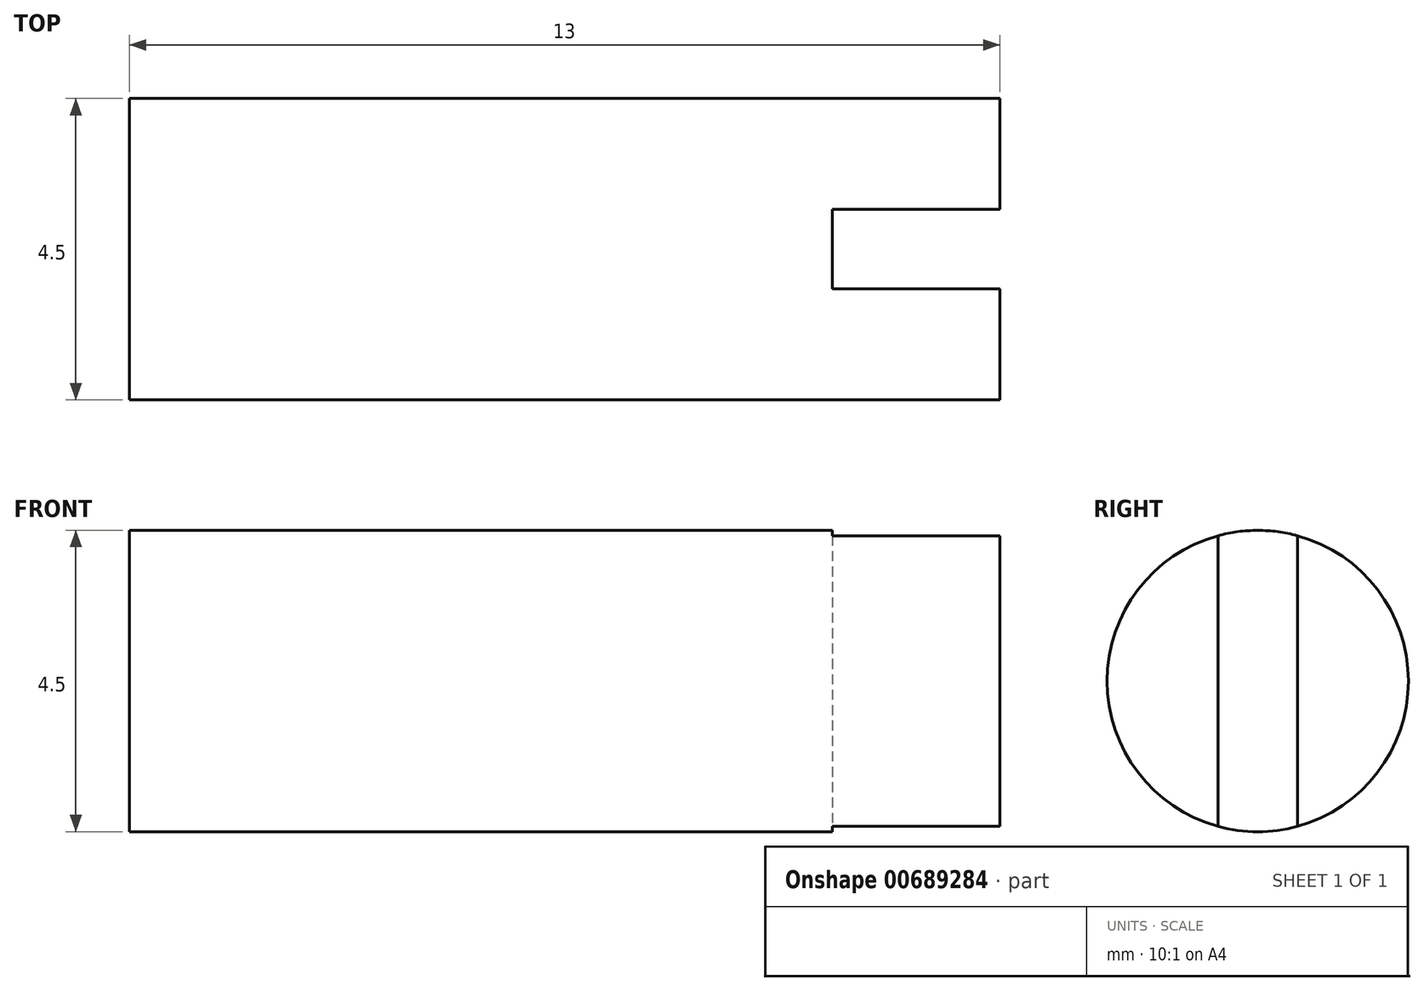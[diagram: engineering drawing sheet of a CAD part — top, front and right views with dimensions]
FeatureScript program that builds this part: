
annotation { "Feature Type Name" : "Feature", "Feature Type Description" : "" }
export const myFeature = defineFeature(function(context is Context, id is Id, definition is map)
    precondition{}
    {
        {
            var Q0;
            Q0=qCreatedBy(makeId("Front.planeOp"),FACE);
            var sketch = newSketch(context, id + "F0", { "sketchPlane" : qUnion([Q0])});
            skLineSegment(sketch, "E0", {"start": v(0, 0) * mm, "end": v(13, 0) * mm});
            skLineSegment(sketch, "E1", {"start": v(13, 0) * mm, "end": v(13, 2.25) * mm});
            skLineSegment(sketch, "E2", {"start": v(13, 2.25) * mm, "end": v(0, 2.25) * mm});
            skLineSegment(sketch, "E3", {"start": v(0, 2.25) * mm, "end": v(0, 0) * mm});
            skSolve(sketch);
        }
        {
            var Q0;
            Q0=makeQuery(id+"F0.imprint","IMPRINT",FACE,{"disambiguationData":[TD([[makeQuery(id+"F0.imprint","IMPRINT",EDGE,{"derivedFrom":sQuery(id+"F0.wireOp",EDGE,"E0")}),1.0]])]});
            var Q1;
            Q1=sQuery(id+"F0.wireOp",EDGE,"E0");
            revolve(context, id + "F1", {"entities" : qUnion([Q0]), "axis" : qUnion([Q1]), "revolveType" : RevolveType.FULL});
        }
        {
            var Q0;
            Q0=makeQuery(id+"F1.opRevolve","SWEPT_FACE",FACE,{"disambiguationData":[OSD([sQuery(id+"F0.wireOp",EDGE,"E1")])]});
            var sketch = newSketch(context, id + "F2", { "sketchPlane" : qUnion([Q0])});
            skLineSegment(sketch, "E4", {"start": v(0.6, 2.17) * mm, "end": v(0.6, -2.17) * mm});
            skLineSegment(sketch, "E5.MirrorCS", {"start": v(-0.6, 2.17) * mm, "end": v(-0.6, -2.17) * mm});
            skSolve(sketch);
        }
        {
            var Q0;
            {var subQ0=sQuery(id+"F2.wireOp",EDGE,"E4");Q0=makeQuery(id+"F2.imprint","IMPRINT",FACE,{"disambiguationData":[TD([[makeQuery(id+"F2.imprint","IMPRINT",EDGE,{"derivedFrom":subQ0}),-1.0]])]});}
            extrude(context, id + "F3", {"entities" : qUnion([Q0]), "operationType" : NewBodyOperationType.REMOVE, "oppositeDirection" : true, "depth" : 2.5 * mm, "offsetDistance" : 25 * mm});
        }
        {
            var Q0;
            Q0=makeQuery(id+"F3.boolean.opBoolean","SPLIT",FACE,{"disambiguationData":[TD([makeQuery(id+"F3.opExtrude","SWEPT_FACE",FACE,{"disambiguationData":[OSD([sQuery(id+"F2.wireOp",EDGE,"E4")])]})])],"derivedFrom":makeQuery(id+"F1.opRevolve","SWEPT_FACE",FACE,{"disambiguationData":[OSD([sQuery(id+"F0.wireOp",EDGE,"E1")])]})});
            var Q1;
            Q1=makeQuery(id+"F1.opRevolve","SWEPT_FACE",FACE,{"disambiguationData":[OSD([sQuery(id+"F0.wireOp",EDGE,"E3")])]});
            cPlane(context, id + "F4", {"entities" : qUnion([Q0, Q1]), "cplaneType" : CPlaneType.MID_PLANE, "offset" : 25 * mm, "width" : 150 * mm, "height" : 150 * mm});
        }
    });
